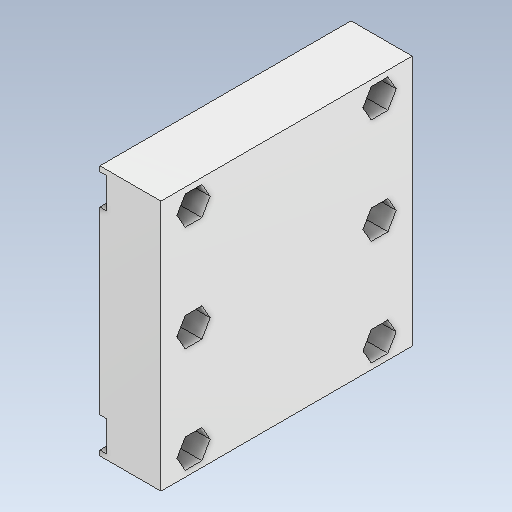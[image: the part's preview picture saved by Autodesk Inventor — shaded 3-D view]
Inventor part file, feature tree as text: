
AUTODESK INVENTOR PART (.ipt)
format: ipt  version: 2020 (Build 240168000, 168)  size: 204,288 bytes
history: native  units: mm
features: extrude x4, sketch x3, other x1
ambient origin geometry x8: Origin, YZ Plane, XZ Plane, XY Plane, X Axis, Y Axis, Z Axis, Center Point
bodies: Body1 (feature_tree)
feature tree (8):
  other  "Bryła1"
  extrude  "Wyciągnięcie proste1"  Depth=74.0mm
  sketch  "Szkic2"
  extrude  "Wyciągnięcie proste2"  Depth=74.0mm
  extrude  "Wyciągnięcie proste3"  Depth=18.0mm TaperAngle=0.0deg
  extrude  "Wyciągnięcie proste4"  Depth=6.0mm
  sketch  "Szkic1"
  sketch  "Szkic3"
